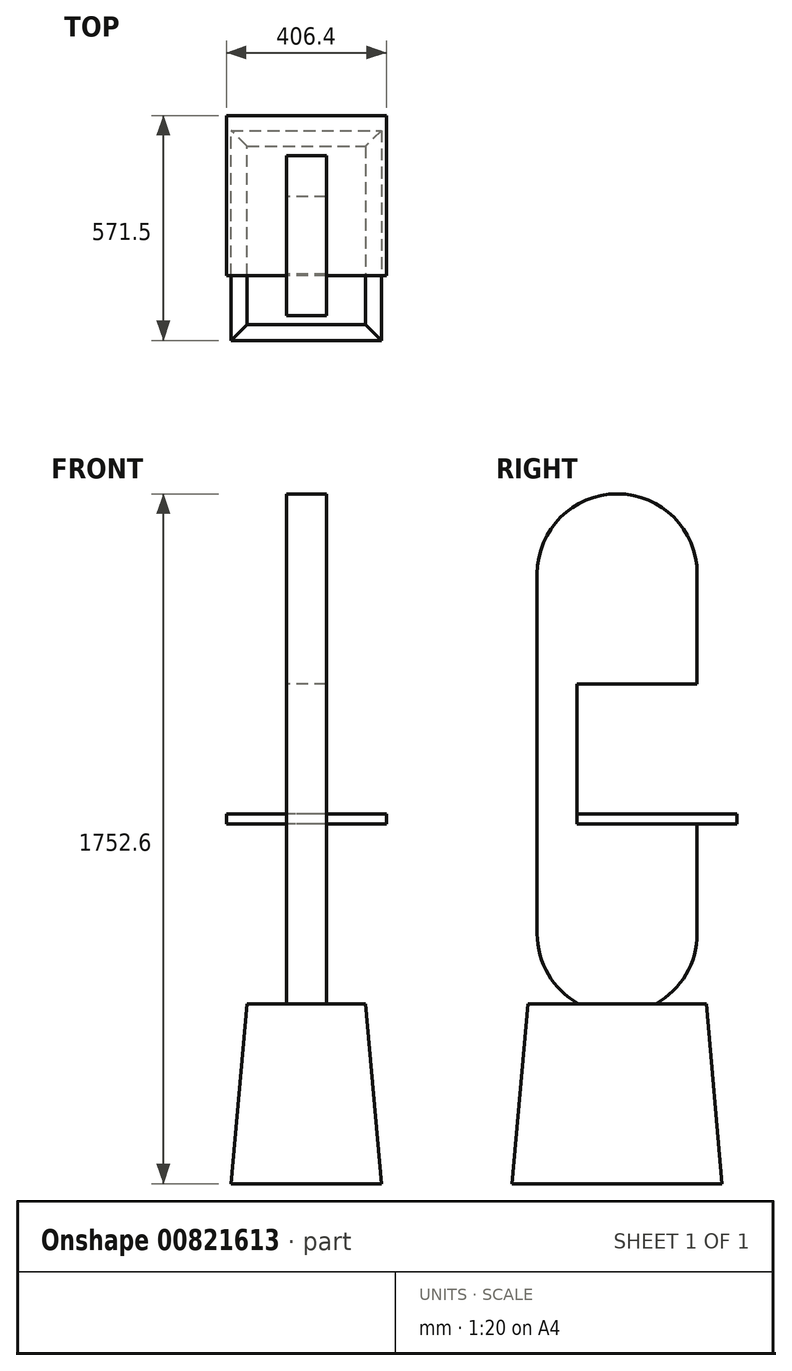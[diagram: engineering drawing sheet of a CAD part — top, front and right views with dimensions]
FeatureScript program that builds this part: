
annotation { "Feature Type Name" : "Feature", "Feature Type Description" : "" }
export const myFeature = defineFeature(function(context is Context, id is Id, definition is map)
    precondition{}
    {
        {
            var Q0;
            Q0=qCreatedBy(makeId("Top.planeOp"),FACE);
            var sketch = newSketch(context, id + "F0", { "sketchPlane" : qUnion([Q0])});
            skLineSegment(sketch, "E0.bottom", {"start": v(-190.5, 0) * mm, "end": v(190.5, 0) * mm});
            skLineSegment(sketch, "E0.top", {"start": v(-190.5, 533.4) * mm, "end": v(190.5, 533.4) * mm});
            skLineSegment(sketch, "E0.left", {"start": v(-190.5, 0) * mm, "end": v(-190.5, 533.4) * mm});
            skLineSegment(sketch, "E0.right", {"start": v(190.5, 0) * mm, "end": v(190.5, 533.4) * mm});
            skSolve(sketch);
        }
        {
            var Q0;
            Q0 = qSketchRegion(id + "F0", true);
            extrude(context, id + "F1", {"entities" : qUnion([Q0]), "depth" : 457.2 * mm, "offsetDistance" : 25.4 * mm, "hasDraft" : true, "draftAngle" : 5 * degree, "draftPullDirection" : true});
        }
        {
            var Q0;
            Q0=qCreatedBy(makeId("Right.planeOp"),FACE);
            var sketch = newSketch(context, id + "F2", { "sketchPlane" : qUnion([Q0])});
            skArc(sketch, "E1", {"start": v(63.5, 635) * mm, "mid": v(266.7, 431.8) * mm, "end": v(469.9, 635) * mm});
            skLineSegment(sketch, "E2", {"start": v(469.9, 635) * mm, "end": v(469.9, 914.4) * mm});
            skLineSegment(sketch, "E3", {"start": v(469.9, 914.4) * mm, "end": v(165.1, 914.4) * mm});
            skLineSegment(sketch, "E4", {"start": v(165.1, 914.4) * mm, "end": v(165.1, 1270) * mm});
            skLineSegment(sketch, "E5", {"start": v(165.1, 1270) * mm, "end": v(469.9, 1270) * mm});
            skLineSegment(sketch, "E6", {"start": v(469.9, 1270) * mm, "end": v(469.9, 1549.4) * mm});
            skArc(sketch, "E7", {"start": v(469.9, 1549.4) * mm, "mid": v(266.7, 1752.6) * mm, "end": v(63.5, 1549.4) * mm});
            skLineSegment(sketch, "E8", {"start": v(63.5, 1549.4) * mm, "end": v(63.5, 635) * mm});
            skLineSegment(sketch, "E9", {"start": v(266.7, 635) * mm, "end": v(266.7, 457.2) * mm, "construction": true});
            skSolve(sketch);
        }
        {
            var Q0;
            Q0 = qSketchRegion(id + "F2", true);
            extrude(context, id + "F3", {"entities" : qUnion([Q0]), "operationType" : NewBodyOperationType.ADD, "depth" : 101.6 * mm, "offsetDistance" : 25.4 * mm, "symmetric" : true});
        }
        {
            var Q0;
            Q0=makeQuery(id+"F3.opExtrude","SWEPT_FACE",FACE,{"disambiguationData":[OSD([sQuery(id+"F2.wireOp",EDGE,"E3")])]});
            var sketch = newSketch(context, id + "F4", { "sketchPlane" : qUnion([Q0])});
            skLineSegment(sketch, "E10.bottom", {"start": v(203.2, 571.5) * mm, "end": v(-203.2, 571.5) * mm});
            skLineSegment(sketch, "E10.top", {"start": v(203.2, 165.1) * mm, "end": v(-203.2, 165.1) * mm});
            skLineSegment(sketch, "E10.left", {"start": v(203.2, 571.5) * mm, "end": v(203.2, 165.1) * mm});
            skLineSegment(sketch, "E10.right", {"start": v(-203.2, 571.5) * mm, "end": v(-203.2, 165.1) * mm});
            skSolve(sketch);
        }
        {
            var Q0;
            Q0 = qSketchRegion(id + "F4", true);
            extrude(context, id + "F5", {"entities" : qUnion([Q0]), "operationType" : NewBodyOperationType.ADD, "depth" : 25.4 * mm, "offsetDistance" : 25.4 * mm});
        }
    });
